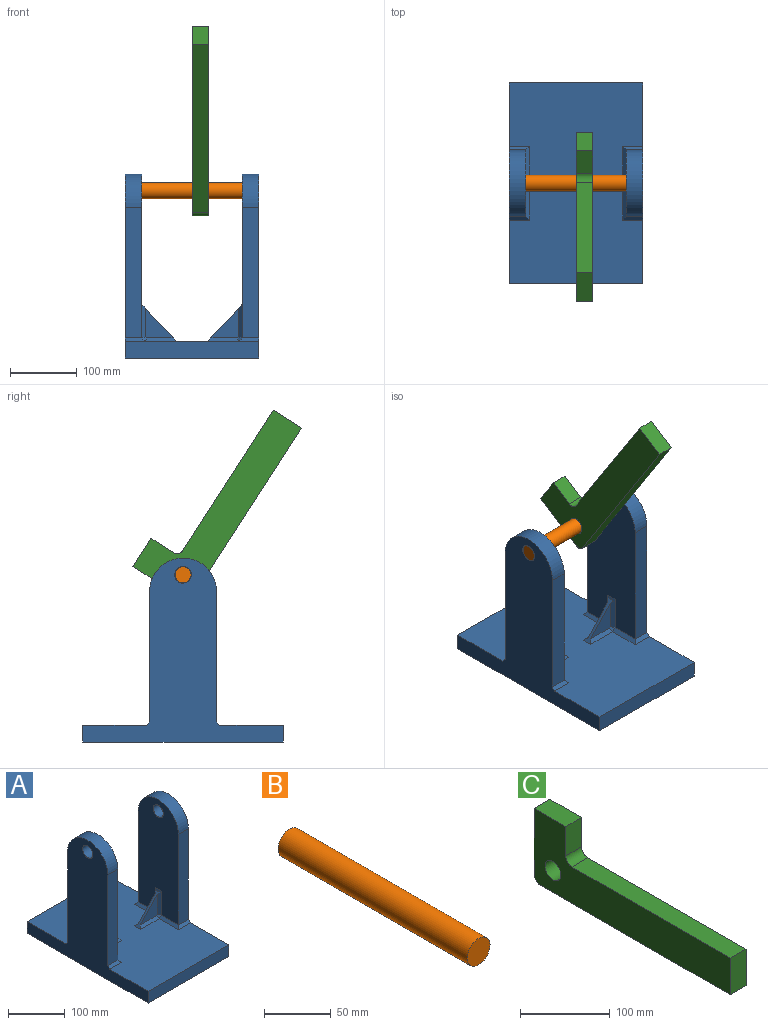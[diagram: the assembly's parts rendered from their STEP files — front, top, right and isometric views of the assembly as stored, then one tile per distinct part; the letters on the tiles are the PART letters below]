
ASSEMBLY  parts=3 mates=4
PART A: 43 faces, bbox 200x300x275 mm
  f0: plane 47.5x5mm, normal (-0.71,0,0.71), area 318.2mm2, adj f1,f12,f20,f42
  f1: plane 300x200mm, normal (0,0,1), area 52010.7mm2, adj f0,f2,f4,f5,f6,f7,f18,f19
  f2: plane 47.5x5mm, normal (0.71,0,0.71), area 318.2mm2, adj f1,f3,f23,f32
  f3: plane 245x100mm, normal (1,0,0), area 22185.4mm2, adj f2,f13,f14,f15,f16,f22,f26,f28
  f4: plane 200x25mm, normal (0,1,0), area 5000mm2, adj f1,f5,f7,f8
  f5: plane 300x275mm, normal (-1,0,0), area 30961.1mm2, adj f1,f4,f6,f8,f13,f14,f15,f16
  f6: plane 200x25mm, normal (0,-1,0), area 5000mm2, adj f1,f5,f7,f8
  f7: plane 300x275mm, normal (1,0,0), area 30961.1mm2, adj f1,f4,f6,f8,f9,f10,f11,f17
  f8: plane 300x200mm, normal (0,0,-1), area 60000mm2, adj f4,f5,f6,f7
  f9: plane 195x25mm, normal (0,-1,0), area 4875mm2, adj f7,f11,f12,f18
  f10: plane 195x25mm, normal (0,1,0), area 4875mm2, adj f7,f11,f12,f20
  f11: cylinder r=50mm len=100mm, axis (1,0,0), area 3927mm2, adj f7,f9,f10,f12
  f12: plane 245x100mm, normal (-1,0,0), area 22155.9mm2, adj f0,f9,f10,f11,f17,f19,f38,f39
  f13: plane 195x25mm, normal (0,-1,0), area 4875mm2, adj f3,f5,f15,f21
  f14: plane 195x25mm, normal (0,1,0), area 4875mm2, adj f3,f5,f15,f23
  f15: cylinder r=50mm len=100mm, axis (1,0,0), area 3927mm2, adj f3,f5,f13,f14
  f16: cylinder r=12.5mm len=25mm, axis (-1,0,0), area 1963.5mm2, adj f3,f5
  f17: cylinder r=12.5mm len=25mm, axis (-1,0,0), area 1963.5mm2, adj f7,f12
  f18: plane 30x5mm, normal (0,-0.71,0.71), area 194.5mm2, adj f1,f7,f9,f19
  f19: plane 47.5x5mm, normal (-0.71,0,0.71), area 318.2mm2, adj f1,f12,f18,f37
  f20: plane 30x5mm, normal (0,0.71,0.71), area 194.5mm2, adj f0,f1,f7,f10
  f21: plane 30x5mm, normal (0,-0.71,0.71), area 194.5mm2, adj f1,f5,f13,f22
  f22: plane 47.5x5mm, normal (0.71,0,0.71), area 318.2mm2, adj f1,f3,f21,f29
  f23: plane 30x5mm, normal (0,0.71,0.71), area 194.5mm2, adj f1,f2,f5,f14
  f24: plane 44.68x41.65mm, normal (0,-1,0), area 928.4mm2, adj f26,f27,f28,f29
  f25: plane 44.68x41.65mm, normal (0,1,0), area 928.4mm2, adj f26,f30,f31,f32
  f26: plane 55.05x51.31mm, normal (0.73,0,0.68), area 447.1mm2, adj f1,f3,f24,f25,f27,f28,f30,f31
  f27: plane 46.31x5mm, normal (0,-0.71,0.71), area 303.7mm2, adj f1,f24,f26,f29
  f28: plane 50.05x5mm, normal (0.71,-0.71,0), area 327.6mm2, adj f3,f24,f26,f29
  f29: plane 7.07x7.07mm, normal (0.5,-0.71,0.5), area 35.4mm2, adj f22,f24,f27,f28
  f30: plane 46.31x5mm, normal (0,0.71,0.71), area 303.7mm2, adj f1,f25,f26,f32
  f31: plane 50.05x5mm, normal (0.71,0.71,0), area 327.6mm2, adj f3,f25,f26,f32
  f32: plane 7.07x7.07mm, normal (0.5,0.71,0.5), area 35.4mm2, adj f2,f25,f30,f31
  f33: plane 44.68x41.65mm, normal (0,1,0), area 928.4mm2, adj f35,f40,f41,f42
  f34: plane 44.68x41.65mm, normal (0,-1,0), area 928.4mm2, adj f35,f36,f37,f38
  f35: plane 53.61x49.97mm, normal (-0.73,0,0.68), area 420.2mm2, adj f1,f33,f34,f36,f38,f39,f40,f41
  f36: plane 46.31x5mm, normal (0,-0.71,0.71), area 303.7mm2, adj f1,f34,f35,f37
  f37: plane 7.07x7.07mm, normal (-0.5,-0.71,0.5), area 35.4mm2, adj f19,f34,f36,f38
  f38: plane 52.01x5mm, normal (-0.71,-0.71,0), area 329.5mm2, adj f12,f34,f35,f37,f39
  f39: plane 15x3.41mm, normal (-0.93,0,0.37), area 50mm2, adj f12,f35,f38,f40
  f40: plane 52.01x5mm, normal (-0.71,0.71,0), area 329.5mm2, adj f12,f33,f35,f39,f42
  f41: plane 46.31x5mm, normal (0,0.71,0.71), area 303.7mm2, adj f1,f33,f35,f42
  f42: plane 7.07x7.07mm, normal (-0.5,0.71,0.5), area 35.4mm2, adj f0,f33,f40,f41
PART B: 3 faces, bbox 24x200x24 mm
  f0: cylinder r=12mm len=200mm, axis (0,1,0), area 15079.6mm2, adj f1,f2
  f1: plane 24x24mm, normal (0,-1,0), area 452.4mm2, adj f0
  f2: plane 24x24mm, normal (0,1,0), area 452.4mm2, adj f0
PART C: 11 faces, bbox 25x310x100 mm
  f0: plane 90x25mm, normal (0,1,0), area 2250mm2, adj f1,f7,f8,f9
  f1: plane 50x25mm, normal (0,0,1), area 1250mm2, adj f0,f2,f8,f9
  f2: plane 40x25mm, normal (0,-1,0), area 1000mm2, adj f1,f3,f8,f9
  f3: cylinder r=10mm len=25mm, axis (-1,0,0), area 392.7mm2, adj f2,f4,f8,f9
  f4: plane 250x25mm, normal (0,0,1), area 6250mm2, adj f3,f5,f8,f9
  f5: plane 50x25mm, normal (0,-1,0), area 1250mm2, adj f4,f6,f8,f9
  f6: plane 300x25mm, normal (0,0,-1), area 7500mm2, adj f5,f7,f8,f9
  f7: cylinder r=10mm len=25mm, axis (-1,0,0), area 392.7mm2, adj f0,f6,f8,f9
  f8: plane 310x100mm, normal (1,0,0), area 17509.1mm2, adj f0,f1,f2,f3,f4,f5,f6,f7
  f9: plane 310x100mm, normal (-1,0,0), area 17509.1mm2, adj f0,f1,f2,f3,f4,f5,f6,f7
  f10: cylinder r=12.5mm len=25mm, axis (-1,0,0), area 1963.5mm2, adj f8,f9
PLACE A t=(-160.14,32.36,62.22)mm fixed
PLACE B rot(axis=(0.69,0.69,-0.21),155.8deg) t=(-160.14,32.36,299.72)mm
PLACE C rot(axis=(-1,0,0),57.2deg) t=(-160.14,23.36,258.26)mm
MATE revolute C.f10 <-> B.f0  axis (-1,0,0) through (-160.14,32.36,299.72)mm
MATE pin_slot A.f16 <-> B.f0  axis (1,0,0) through (-60.14,32.36,299.72)mm
MATE cylindrical B.f0 <-> A.f16  axis (1,0,0) through (-260.14,32.36,299.72)mm
MATE cylindrical B.f0 <-> A.f16  axis (1,0,0) through (-160.14,32.36,299.72)mm
